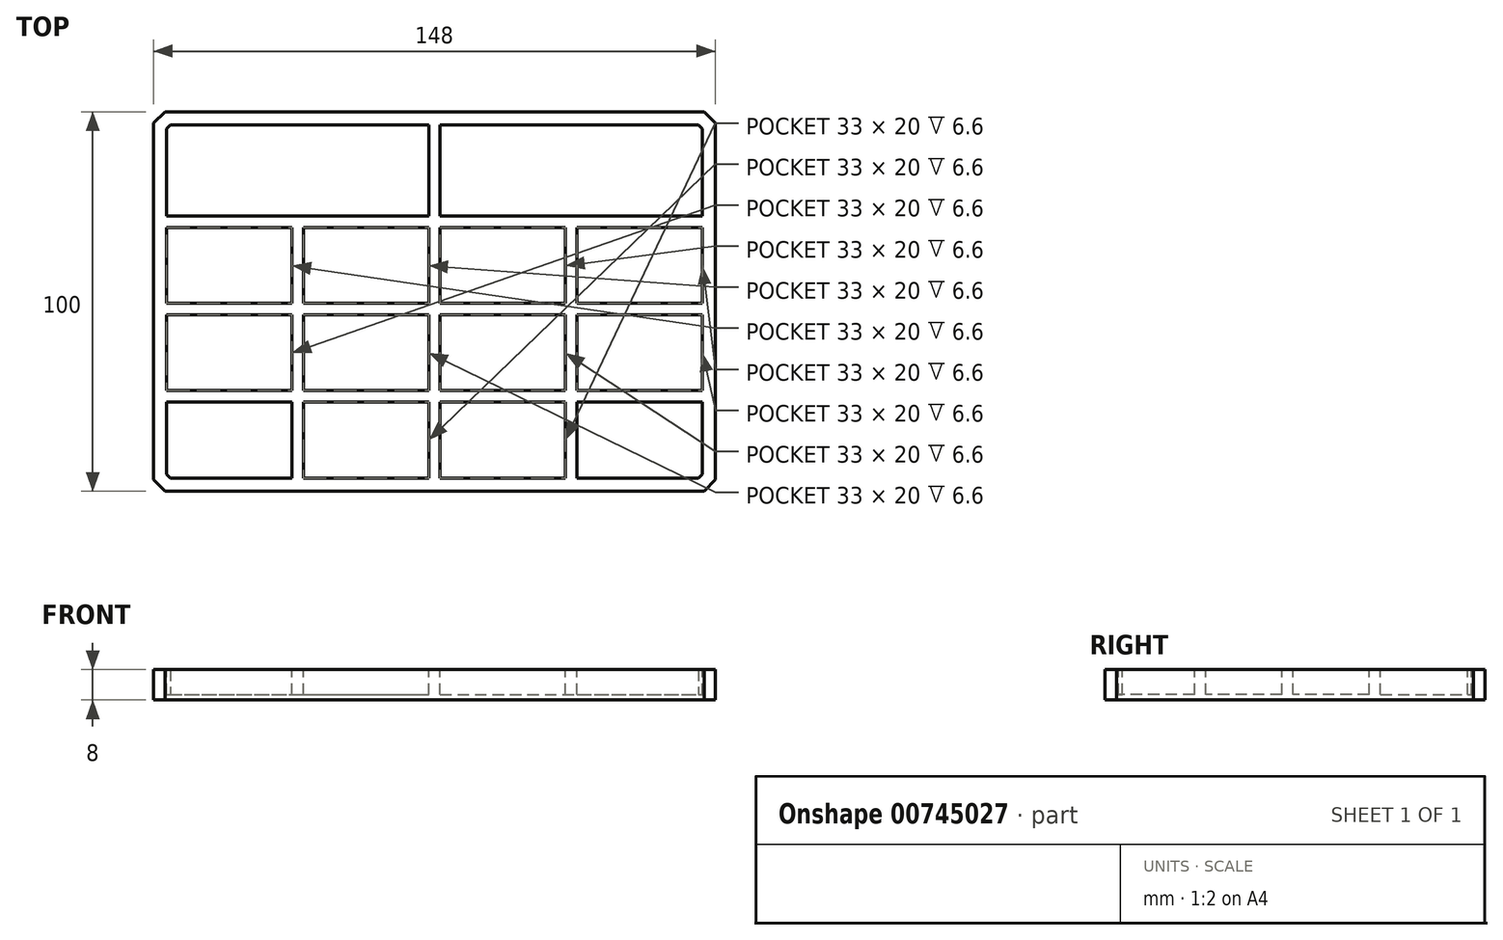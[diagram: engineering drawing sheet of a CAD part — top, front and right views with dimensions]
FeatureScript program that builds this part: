
annotation { "Feature Type Name" : "Feature", "Feature Type Description" : "" }
export const myFeature = defineFeature(function(context is Context, id is Id, definition is map)
    precondition{}
    {
        {
            var Q0;
            Q0=qCreatedBy(makeId("Top.planeOp"),FACE);
            var sketch = newSketch(context, id + "F0", { "sketchPlane" : qUnion([Q0])});
            skLineSegment(sketch, "E0.bottom", {"start": v(74, -50) * mm, "end": v(-74, -50) * mm});
            skLineSegment(sketch, "E0.top", {"start": v(74, 50) * mm, "end": v(-74, 50) * mm});
            skLineSegment(sketch, "E0.left", {"start": v(74, -50) * mm, "end": v(74, 50) * mm});
            skLineSegment(sketch, "E0.right", {"start": v(-74, -50) * mm, "end": v(-74, 50) * mm});
            skPoint(sketch, "E0.middle", {"position": v(0, 0) * mm});
            skSolve(sketch);
        }
        {
            var Q0;
            Q0=makeQuery(id+"F0.imprint","IMPRINT",FACE,{"disambiguationData":[TD([[makeQuery(id+"F0.imprint","IMPRINT",EDGE,{"derivedFrom":sQuery(id+"F0.wireOp",EDGE,"E0.bottom")}),-1.0]])]});
            extrude(context, id + "F1", {"entities" : qUnion([Q0]), "depth" : 8 * mm, "offsetDistance" : 25 * mm});
        }
        {
            var Q0;
            Q0=makeQuery(id+"F1.opExtrude","SWEPT_EDGE",EDGE,{"disambiguationData":[OSD([sQuery(id+"F0.wireOp",EDGE,"E0.bottom"),sQuery(id+"F0.wireOp",EDGE,"E0.right")])]});
            var Q1;
            Q1=makeQuery(id+"F1.opExtrude","SWEPT_EDGE",EDGE,{"disambiguationData":[OSD([sQuery(id+"F0.wireOp",EDGE,"E0.top"),sQuery(id+"F0.wireOp",EDGE,"E0.right")])]});
            var Q2;
            Q2=makeQuery(id+"F1.opExtrude","SWEPT_EDGE",EDGE,{"disambiguationData":[OSD([sQuery(id+"F0.wireOp",EDGE,"E0.top"),sQuery(id+"F0.wireOp",EDGE,"E0.left")])]});
            var Q3;
            Q3=makeQuery(id+"F1.opExtrude","SWEPT_EDGE",EDGE,{"disambiguationData":[OSD([sQuery(id+"F0.wireOp",EDGE,"E0.bottom"),sQuery(id+"F0.wireOp",EDGE,"E0.left")])]});
            chamfer(context, id + "F2", {"entities" : qUnion([Q0, Q1, Q2, Q3]), "width" : 3 * mm, "tangentPropagation" : true});
        }
        {
            var Q0;
            Q0=makeQuery(id+"F1.opExtrude","CAP_FACE",FACE,{"disambiguationData":[OSD([sQuery(id+"F0.wireOp",EDGE,"E0.bottom"),sQuery(id+"F0.wireOp",EDGE,"E0.top"),sQuery(id+"F0.wireOp",EDGE,"E0.left"),sQuery(id+"F0.wireOp",EDGE,"E0.right")])],"isStart":false});
            var sketch = newSketch(context, id + "F3", { "sketchPlane" : qUnion([Q0])});
            skLineSegment(sketch, "E1.bottom", {"start": v(-70.5, -26.5) * mm, "end": v(-37.5, -26.5) * mm});
            skLineSegment(sketch, "E1.top", {"start": v(-70.5, -46.5) * mm, "end": v(-37.5, -46.5) * mm});
            skLineSegment(sketch, "E1.left", {"start": v(-70.5, -26.5) * mm, "end": v(-70.5, -46.5) * mm});
            skLineSegment(sketch, "E1.right", {"start": v(-37.5, -26.5) * mm, "end": v(-37.5, -46.5) * mm});
            skLineSegment(sketch, "E2.1.0.0", {"start": v(-34.5, -26.5) * mm, "end": v(-1.5, -26.5) * mm});
            skLineSegment(sketch, "E2.1.0.1", {"start": v(-34.5, -26.5) * mm, "end": v(-34.5, -46.5) * mm});
            skLineSegment(sketch, "E2.1.0.2", {"start": v(-34.5, -46.5) * mm, "end": v(-1.5, -46.5) * mm});
            skLineSegment(sketch, "E2.1.0.3", {"start": v(-1.5, -26.5) * mm, "end": v(-1.5, -46.5) * mm});
            skLineSegment(sketch, "E2.2.0.0", {"start": v(1.5, -26.5) * mm, "end": v(34.5, -26.5) * mm});
            skLineSegment(sketch, "E2.2.0.1", {"start": v(1.5, -26.5) * mm, "end": v(1.5, -46.5) * mm});
            skLineSegment(sketch, "E2.2.0.2", {"start": v(1.5, -46.5) * mm, "end": v(34.5, -46.5) * mm});
            skLineSegment(sketch, "E2.2.0.3", {"start": v(34.5, -26.5) * mm, "end": v(34.5, -46.5) * mm});
            skLineSegment(sketch, "E2.3.0.0", {"start": v(37.5, -26.5) * mm, "end": v(70.5, -26.5) * mm});
            skLineSegment(sketch, "E2.3.0.1", {"start": v(37.5, -26.5) * mm, "end": v(37.5, -46.5) * mm});
            skLineSegment(sketch, "E2.3.0.2", {"start": v(37.5, -46.5) * mm, "end": v(70.5, -46.5) * mm});
            skLineSegment(sketch, "E2.3.0.3", {"start": v(70.5, -26.5) * mm, "end": v(70.5, -46.5) * mm});
            skLineSegment(sketch, "E2.direction1", {"start": v(-70.5, -26.5) * mm, "end": v(-34.5, -26.5) * mm, "construction": true});
            skLineSegment(sketch, "E3.0.1.0", {"start": v(-37.5, -3.5) * mm, "end": v(-37.5, -23.5) * mm});
            skLineSegment(sketch, "E3.0.1.1", {"start": v(-70.5, -3.5) * mm, "end": v(-70.5, -23.5) * mm});
            skLineSegment(sketch, "E3.0.1.2", {"start": v(-70.5, -23.5) * mm, "end": v(-37.5, -23.5) * mm});
            skLineSegment(sketch, "E3.0.1.3", {"start": v(-70.5, -3.5) * mm, "end": v(-34.5, -3.5) * mm, "construction": true});
            skLineSegment(sketch, "E3.0.1.4", {"start": v(-34.5, -3.5) * mm, "end": v(-1.5, -3.5) * mm});
            skLineSegment(sketch, "E3.0.1.5", {"start": v(-34.5, -23.5) * mm, "end": v(-1.5, -23.5) * mm});
            skLineSegment(sketch, "E3.0.1.6", {"start": v(-34.5, -3.5) * mm, "end": v(-34.5, -23.5) * mm});
            skLineSegment(sketch, "E3.0.1.7", {"start": v(-1.5, -3.5) * mm, "end": v(-1.5, -23.5) * mm});
            skLineSegment(sketch, "E3.0.1.8", {"start": v(1.5, -3.5) * mm, "end": v(1.5, -23.5) * mm});
            skLineSegment(sketch, "E3.0.1.9", {"start": v(1.5, -3.5) * mm, "end": v(34.5, -3.5) * mm});
            skLineSegment(sketch, "E3.0.1.10", {"start": v(1.5, -23.5) * mm, "end": v(34.5, -23.5) * mm});
            skLineSegment(sketch, "E3.0.1.11", {"start": v(34.5, -3.5) * mm, "end": v(34.5, -23.5) * mm});
            skLineSegment(sketch, "E3.0.1.12", {"start": v(37.5, -3.5) * mm, "end": v(37.5, -23.5) * mm});
            skLineSegment(sketch, "E3.0.1.13", {"start": v(37.5, -3.5) * mm, "end": v(70.5, -3.5) * mm});
            skLineSegment(sketch, "E3.0.1.14", {"start": v(70.5, -3.5) * mm, "end": v(70.5, -23.5) * mm});
            skLineSegment(sketch, "E3.0.1.15", {"start": v(37.5, -23.5) * mm, "end": v(70.5, -23.5) * mm});
            skLineSegment(sketch, "E3.0.2.0", {"start": v(-37.5, 19.5) * mm, "end": v(-37.5, -0.5) * mm});
            skLineSegment(sketch, "E3.0.2.1", {"start": v(-70.5, 19.5) * mm, "end": v(-70.5, -0.5) * mm});
            skLineSegment(sketch, "E3.0.2.2", {"start": v(-70.5, -0.5) * mm, "end": v(-37.5, -0.5) * mm});
            skLineSegment(sketch, "E3.0.2.3", {"start": v(-70.5, 19.5) * mm, "end": v(-34.5, 19.5) * mm, "construction": true});
            skLineSegment(sketch, "E3.0.2.4", {"start": v(-34.5, 19.5) * mm, "end": v(-1.5, 19.5) * mm});
            skLineSegment(sketch, "E3.0.2.5", {"start": v(-34.5, -0.5) * mm, "end": v(-1.5, -0.5) * mm});
            skLineSegment(sketch, "E3.0.2.6", {"start": v(-34.5, 19.5) * mm, "end": v(-34.5, -0.5) * mm});
            skLineSegment(sketch, "E3.0.2.7", {"start": v(-1.5, 19.5) * mm, "end": v(-1.5, -0.5) * mm});
            skLineSegment(sketch, "E3.0.2.8", {"start": v(1.5, 19.5) * mm, "end": v(1.5, -0.5) * mm});
            skLineSegment(sketch, "E3.0.2.9", {"start": v(1.5, 19.5) * mm, "end": v(34.5, 19.5) * mm});
            skLineSegment(sketch, "E3.0.2.10", {"start": v(1.5, -0.5) * mm, "end": v(34.5, -0.5) * mm});
            skLineSegment(sketch, "E3.0.2.11", {"start": v(34.5, 19.5) * mm, "end": v(34.5, -0.5) * mm});
            skLineSegment(sketch, "E3.0.2.12", {"start": v(37.5, 19.5) * mm, "end": v(37.5, -0.5) * mm});
            skLineSegment(sketch, "E3.0.2.13", {"start": v(37.5, 19.5) * mm, "end": v(70.5, 19.5) * mm});
            skLineSegment(sketch, "E3.0.2.14", {"start": v(70.5, 19.5) * mm, "end": v(70.5, -0.5) * mm});
            skLineSegment(sketch, "E3.0.2.15", {"start": v(37.5, -0.5) * mm, "end": v(70.5, -0.5) * mm});
            skLineSegment(sketch, "E3.direction1", {"start": v(-37.5, -46.5) * mm, "end": v(-12.5, -46.5) * mm, "construction": true});
            skLineSegment(sketch, "E3.direction2", {"start": v(-37.5, -46.5) * mm, "end": v(-37.5, -23.5) * mm, "construction": true});
            skLineSegment(sketch, "E4", {"start": v(-70.5, 19.5) * mm, "end": v(-37.5, 19.5) * mm});
            skLineSegment(sketch, "E5", {"start": v(-70.5, -3.5) * mm, "end": v(-37.5, -3.5) * mm});
            skLineSegment(sketch, "E6.bottom", {"start": v(-70.5, 22.5) * mm, "end": v(-1.5, 22.5) * mm});
            skLineSegment(sketch, "E6.top", {"start": v(-70.5, 46.5) * mm, "end": v(-1.5, 46.5) * mm});
            skLineSegment(sketch, "E6.left", {"start": v(-70.5, 22.5) * mm, "end": v(-70.5, 46.5) * mm});
            skLineSegment(sketch, "E6.right", {"start": v(-1.5, 22.5) * mm, "end": v(-1.5, 46.5) * mm});
            skLineSegment(sketch, "E7.bottom", {"start": v(1.5, 22.5) * mm, "end": v(70.5, 22.5) * mm});
            skLineSegment(sketch, "E7.top", {"start": v(1.5, 46.5) * mm, "end": v(70.5, 46.5) * mm});
            skLineSegment(sketch, "E7.left", {"start": v(1.5, 22.5) * mm, "end": v(1.5, 46.5) * mm});
            skLineSegment(sketch, "E7.right", {"start": v(70.5, 22.5) * mm, "end": v(70.5, 46.5) * mm});
            skSolve(sketch);
        }
        {
            var Q0;
            Q0=makeQuery(id+"F3.imprint","IMPRINT",FACE,{"disambiguationData":[TD([[makeQuery(id+"F3.imprint","IMPRINT",EDGE,{"derivedFrom":sQuery(id+"F3.wireOp",EDGE,"E6.bottom")}),1.0]])]});
            var Q1;
            Q1=makeQuery(id+"F3.imprint","IMPRINT",FACE,{"disambiguationData":[TD([[makeQuery(id+"F3.imprint","IMPRINT",EDGE,{"derivedFrom":sQuery(id+"F3.wireOp",EDGE,"E7.bottom")}),1.0]])]});
            var Q2;
            Q2=makeQuery(id+"F3.imprint","IMPRINT",FACE,{"disambiguationData":[TD([[makeQuery(id+"F3.imprint","IMPRINT",EDGE,{"derivedFrom":sQuery(id+"F3.wireOp",EDGE,"E3.0.2.0")}),-1.0]])]});
            var Q3;
            Q3=makeQuery(id+"F3.imprint","IMPRINT",FACE,{"disambiguationData":[TD([[makeQuery(id+"F3.imprint","IMPRINT",EDGE,{"derivedFrom":sQuery(id+"F3.wireOp",EDGE,"E3.0.2.4")}),-1.0]])]});
            var Q4;
            Q4=makeQuery(id+"F3.imprint","IMPRINT",FACE,{"disambiguationData":[TD([[makeQuery(id+"F3.imprint","IMPRINT",EDGE,{"derivedFrom":sQuery(id+"F3.wireOp",EDGE,"E3.0.2.8")}),1.0]])]});
            var Q5;
            Q5=makeQuery(id+"F3.imprint","IMPRINT",FACE,{"disambiguationData":[TD([[makeQuery(id+"F3.imprint","IMPRINT",EDGE,{"derivedFrom":sQuery(id+"F3.wireOp",EDGE,"E3.0.2.12")}),1.0]])]});
            var Q6;
            Q6=makeQuery(id+"F3.imprint","IMPRINT",FACE,{"disambiguationData":[TD([[makeQuery(id+"F3.imprint","IMPRINT",EDGE,{"derivedFrom":sQuery(id+"F3.wireOp",EDGE,"E3.0.1.12")}),1.0]])]});
            var Q7;
            Q7=makeQuery(id+"F3.imprint","IMPRINT",FACE,{"disambiguationData":[TD([[makeQuery(id+"F3.imprint","IMPRINT",EDGE,{"derivedFrom":sQuery(id+"F3.wireOp",EDGE,"E3.0.1.8")}),1.0]])]});
            var Q8;
            Q8=makeQuery(id+"F3.imprint","IMPRINT",FACE,{"disambiguationData":[TD([[makeQuery(id+"F3.imprint","IMPRINT",EDGE,{"derivedFrom":sQuery(id+"F3.wireOp",EDGE,"E3.0.1.4")}),-1.0]])]});
            var Q9;
            Q9=makeQuery(id+"F3.imprint","IMPRINT",FACE,{"disambiguationData":[TD([[makeQuery(id+"F3.imprint","IMPRINT",EDGE,{"derivedFrom":sQuery(id+"F3.wireOp",EDGE,"E3.0.1.0")}),-1.0]])]});
            var Q10;
            Q10=makeQuery(id+"F3.imprint","IMPRINT",FACE,{"disambiguationData":[TD([[makeQuery(id+"F3.imprint","IMPRINT",EDGE,{"derivedFrom":sQuery(id+"F3.wireOp",EDGE,"E1.bottom")}),-1.0]])]});
            var Q11;
            Q11=makeQuery(id+"F3.imprint","IMPRINT",FACE,{"disambiguationData":[TD([[makeQuery(id+"F3.imprint","IMPRINT",EDGE,{"derivedFrom":sQuery(id+"F3.wireOp",EDGE,"E2.1.0.0")}),-1.0]])]});
            var Q12;
            Q12=makeQuery(id+"F3.imprint","IMPRINT",FACE,{"disambiguationData":[TD([[makeQuery(id+"F3.imprint","IMPRINT",EDGE,{"derivedFrom":sQuery(id+"F3.wireOp",EDGE,"E2.2.0.0")}),-1.0]])]});
            var Q13;
            Q13=makeQuery(id+"F3.imprint","IMPRINT",FACE,{"disambiguationData":[TD([[makeQuery(id+"F3.imprint","IMPRINT",EDGE,{"derivedFrom":sQuery(id+"F3.wireOp",EDGE,"E2.3.0.0")}),-1.0]])]});
            extrude(context, id + "F4", {"entities" : qUnion([Q0, Q1, Q2, Q3, Q4, Q5, Q6, Q7, Q8, Q9, Q10, Q11, Q12, Q13]), "operationType" : NewBodyOperationType.REMOVE, "oppositeDirection" : true, "depth" : 6.6 * mm, "offsetDistance" : 25 * mm});
        }
        {
            var Q0;
            Q0=makeQuery(id+"F4.boolean.opBoolean","COPY",EDGE,{"derivedFrom":makeQuery(id+"F4.opExtrude","SWEPT_EDGE",EDGE,{"disambiguationData":[OSD([sQuery(id+"F3.wireOp",EDGE,"E7.top"),sQuery(id+"F3.wireOp",EDGE,"E7.right")])]})});
            var Q1;
            Q1=makeQuery(id+"F4.boolean.opBoolean","COPY",EDGE,{"derivedFrom":makeQuery(id+"F4.opExtrude","SWEPT_EDGE",EDGE,{"disambiguationData":[OSD([sQuery(id+"F3.wireOp",EDGE,"E6.top"),sQuery(id+"F3.wireOp",EDGE,"E6.left")])]})});
            var Q2;
            Q2=makeQuery(id+"F4.boolean.opBoolean","COPY",EDGE,{"derivedFrom":makeQuery(id+"F4.opExtrude","SWEPT_EDGE",EDGE,{"disambiguationData":[OSD([sQuery(id+"F3.wireOp",EDGE,"E2.3.0.2"),sQuery(id+"F3.wireOp",EDGE,"E2.3.0.3")])]})});
            var Q3;
            Q3=makeQuery(id+"F4.boolean.opBoolean","COPY",EDGE,{"derivedFrom":makeQuery(id+"F4.opExtrude","SWEPT_EDGE",EDGE,{"disambiguationData":[OSD([sQuery(id+"F3.wireOp",EDGE,"E1.top"),sQuery(id+"F3.wireOp",EDGE,"E1.left")])]})});
            chamfer(context, id + "F5", {"entities" : qUnion([Q0, Q1, Q2, Q3]), "width" : 1 * mm, "tangentPropagation" : true});
        }
    });
